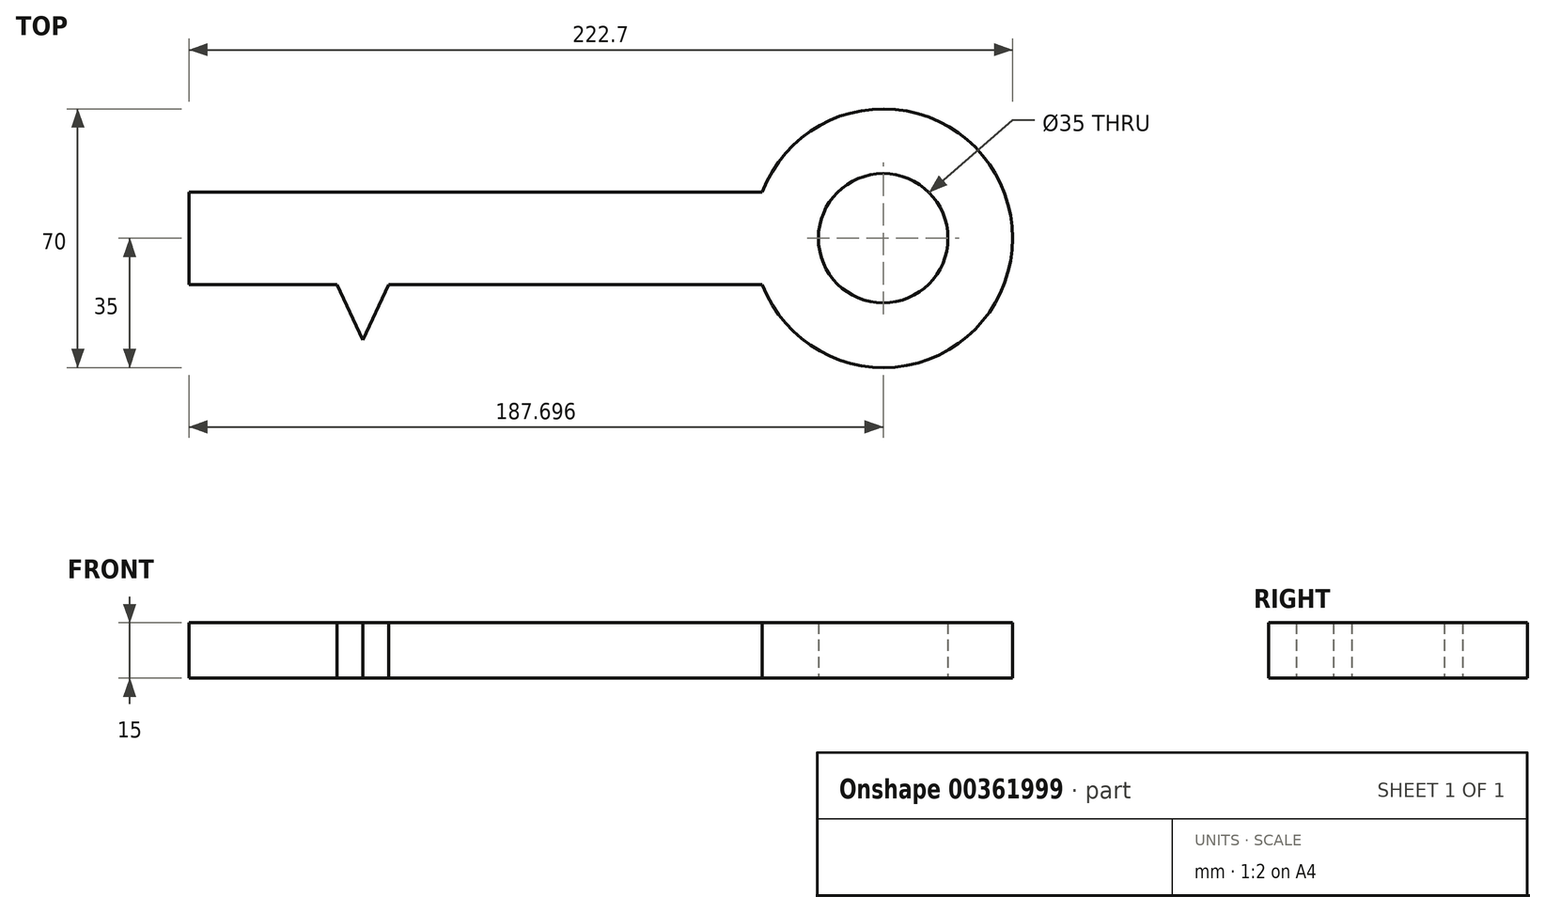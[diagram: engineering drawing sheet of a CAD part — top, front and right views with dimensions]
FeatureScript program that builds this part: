
annotation { "Feature Type Name" : "Feature", "Feature Type Description" : "" }
export const myFeature = defineFeature(function(context is Context, id is Id, definition is map)
    precondition{}
    {
        {
            var Q0;
            Q0=qCreatedBy(makeId("Top.planeOp"),FACE);
            var sketch = newSketch(context, id + "F0", { "sketchPlane" : qUnion([Q0])});
            skLineSegment(sketch, "E0.bottom", {"start": v(-71.35, 15) * mm, "end": v(83.65, 15) * mm});
            skLineSegment(sketch, "E0.top", {"start": v(-71.35, 40) * mm, "end": v(83.65, 40) * mm});
            skLineSegment(sketch, "E0.left", {"start": v(-71.35, 15) * mm, "end": v(-71.35, 40) * mm});
            skLineSegment(sketch, "E0.right", {"start": v(83.65, 15) * mm, "end": v(83.65, 40) * mm});
            skPoint(sketch, "E1.oppositeSnap0", {"position": v(6.15, 40) * mm});
            skLineSegment(sketch, "E2.bottom", {"start": v(-71.35, 15) * mm, "end": v(-61.35, 15) * mm});
            skLineSegment(sketch, "E2.top", {"start": v(-71.35, -15) * mm, "end": v(-61.35, -15) * mm});
            skLineSegment(sketch, "E2.left", {"start": v(-71.35, 15) * mm, "end": v(-71.35, -15) * mm});
            skLineSegment(sketch, "E2.right", {"start": v(-61.35, 15) * mm, "end": v(-61.35, -15) * mm});
            skLineSegment(sketch, "E3.bottom", {"start": v(-51.35, 15) * mm, "end": v(-41.35, 15) * mm});
            skLineSegment(sketch, "E3.top", {"start": v(-51.35, 0) * mm, "end": v(-41.35, 0) * mm});
            skLineSegment(sketch, "E3.left", {"start": v(-51.35, 15) * mm, "end": v(-51.35, 0) * mm});
            skLineSegment(sketch, "E3.right", {"start": v(-41.35, 15) * mm, "end": v(-41.35, 0) * mm});
            skLineSegment(sketch, "E4", {"start": v(-31.35, 15) * mm, "end": v(-24.35, 0) * mm});
            skLineSegment(sketch, "E5", {"start": v(-24.35, 0) * mm, "end": v(-17.35, 15) * mm});
            skArc(sketch, "E6", {"start": v(83.65, 15) * mm, "mid": v(151.35, 27.5) * mm, "end": v(83.65, 40) * mm});
            skCircle(sketch, "E7", {"center": v(116.35, 27.5) * mm, "radius": 17.5 * mm});
            skLineSegment(sketch, "E8", {"start": v(116.35, 27.5) * mm, "end": v(-71.35, 27.5) * mm, "construction": true});
            skSolve(sketch);
        }
        {
            var Q0;
            Q0=makeQuery(id+"F0.imprint","IMPRINT",FACE,{"disambiguationData":[TD([[makeQuery(id+"F0.imprint","IMPRINT",EDGE,{"derivedFrom":sQuery(id+"F0.wireOp",EDGE,"E0.top")}),-1.0]])]});
            var Q1;
            Q1=makeQuery(id+"F0.imprint","IMPRINT",FACE,{"disambiguationData":[TD([[makeQuery(id+"F0.imprint","IMPRINT",EDGE,{"derivedFrom":sQuery(id+"F0.wireOp",EDGE,"E0.right")}),-1.0]])]});
            var Q2;
            Q2=makeQuery(id+"F0.imprint","IMPRINT",FACE,{"disambiguationData":[TD([[makeQuery(id+"F0.imprint","IMPRINT",EDGE,{"derivedFrom":sQuery(id+"F0.wireOp",EDGE,"E2.bottom")}),-1.0]])]});
            var Q3;
            Q3=makeQuery(id+"F0.imprint","IMPRINT",FACE,{"disambiguationData":[TD([[makeQuery(id+"F0.imprint","IMPRINT",EDGE,{"derivedFrom":sQuery(id+"F0.wireOp",EDGE,"E3.bottom")}),-1.0]])]});
            var Q4;
            {var subQ0=sQuery(id+"F0.wireOp",EDGE,"E4");Q4=makeQuery(id+"F0.imprint","IMPRINT",FACE,{"disambiguationData":[TD([[makeQuery(id+"F0.imprint","IMPRINT",EDGE,{"derivedFrom":subQ0}),1.0]])]});}
            extrude(context, id + "F1", {"entities" : qUnion([Q0, Q1, Q2, Q3, Q4]), "depth" : 15 * mm});
        }
    });
